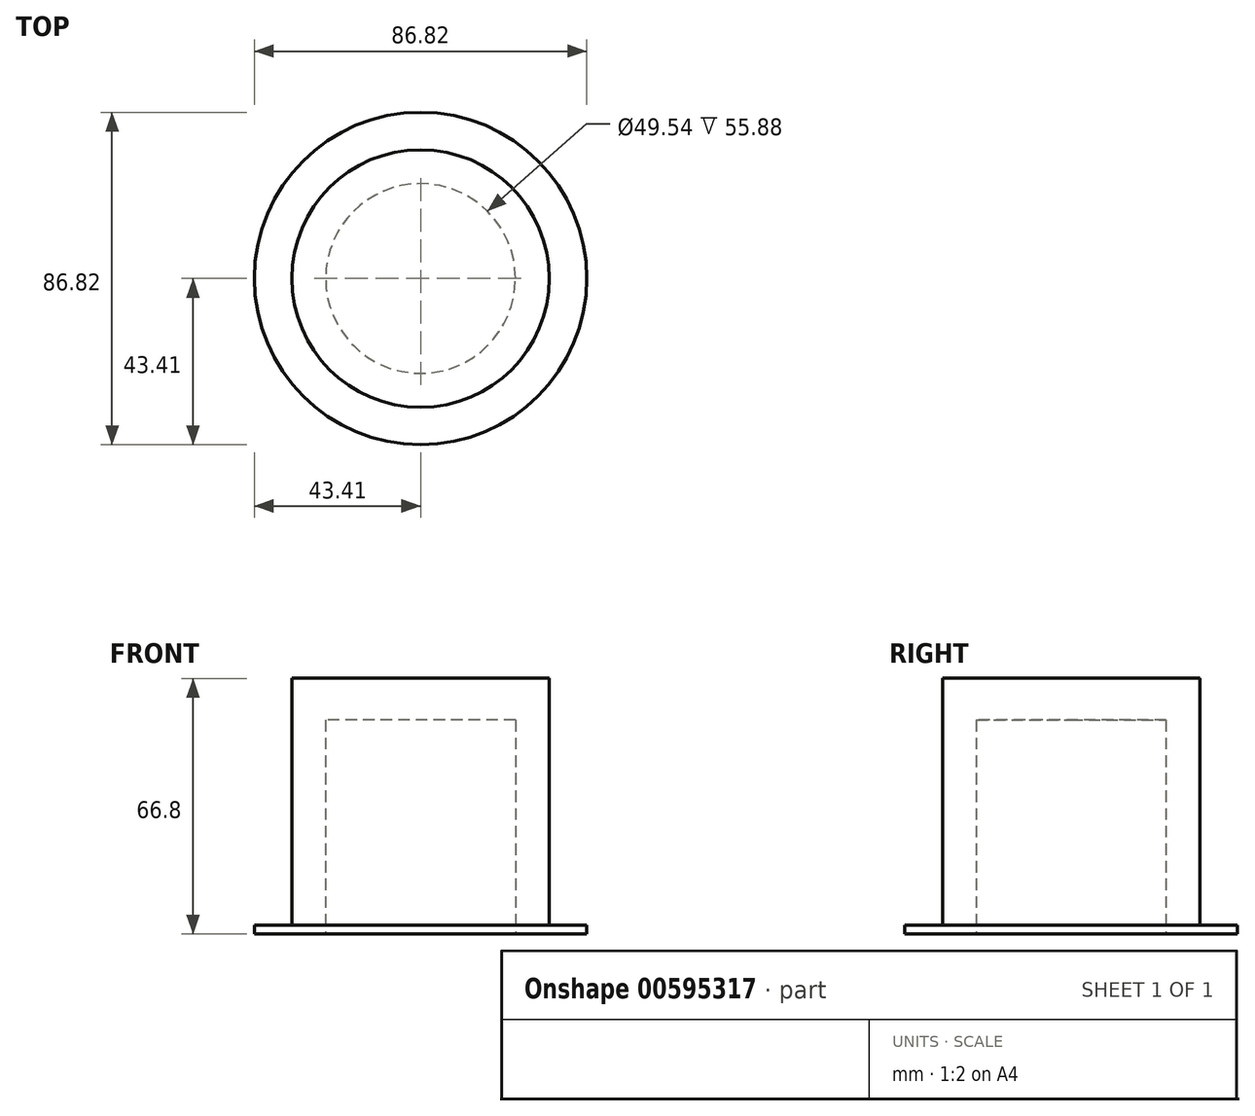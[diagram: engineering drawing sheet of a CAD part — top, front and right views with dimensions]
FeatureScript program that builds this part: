
annotation { "Feature Type Name" : "Feature", "Feature Type Description" : "" }
export const myFeature = defineFeature(function(context is Context, id is Id, definition is map)
    precondition{}
    {
        {
            var Q0;
            Q0=qCreatedBy(makeId("Top.planeOp"),FACE);
            var sketch = newSketch(context, id + "F0", { "sketchPlane" : qUnion([Q0])});
            skCircle(sketch, "E0", {"center": v(0, 0) * mm, "radius": 43.41 * mm});
            skSolve(sketch);
        }
        {
            var Q0;
            Q0 = qSketchRegion(id + "F0", true);
            extrude(context, id + "F1", {"entities" : qUnion([Q0]), "depth" : 2.3 * mm, "offsetDistance" : 25.4 * mm});
        }
        {
            var Q0;
            Q0=makeQuery(id+"F1.opExtrude","CAP_FACE",FACE,{"disambiguationData":[OSD([sQuery(id+"F0.wireOp",EDGE,"E0")])],"isStart":false});
            var sketch = newSketch(context, id + "F2", { "sketchPlane" : qUnion([Q0])});
            skCircle(sketch, "E1", {"center": v(0, 0) * mm, "radius": 33.61 * mm});
            skSolve(sketch);
        }
        {
            var Q0;
            Q0 = qSketchRegion(id + "F2", true);
            extrude(context, id + "F3", {"entities" : qUnion([Q0]), "operationType" : NewBodyOperationType.ADD, "depth" : 64.52 * mm, "offsetDistance" : 25.4 * mm});
        }
        {
            var Q0;
            Q0=qCreatedBy(makeId("Top.planeOp"),FACE);
            var sketch = newSketch(context, id + "F4", { "sketchPlane" : qUnion([Q0])});
            skCircle(sketch, "E2", {"center": v(0, 0) * mm, "radius": 24.77 * mm});
            skSolve(sketch);
        }
        {
            var Q0;
            Q0 = qSketchRegion(id + "F4", true);
            extrude(context, id + "F5", {"entities" : qUnion([Q0]), "operationType" : NewBodyOperationType.REMOVE, "depth" : 55.88 * mm, "offsetDistance" : 25.4 * mm});
        }
    });
